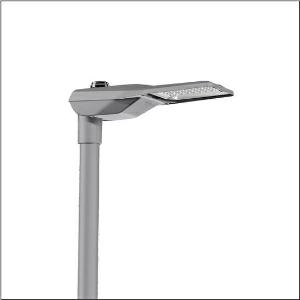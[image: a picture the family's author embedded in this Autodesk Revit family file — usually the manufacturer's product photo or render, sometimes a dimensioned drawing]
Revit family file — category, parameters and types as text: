
# Revit family: streetlight_sl_21_mini___st1_0a_5xe6d37n08jb_4401
name_source: partatom
category: Lighting Fixtures
units: mm (PartAtom-declared; Revit-internal decimal feet)

## family parameters
Cut with Voids When Loaded = No
Host = Face
Light Source = No
Part Type = Normal
Room Calculation Point = No
Round Connector Dimension = Use Diameter
Shared = No

## types (1)
- --- (1 x LED, 12830 lm, 87.3 W, 3000K)
    Apparent Load = 87 VA
    CIE Flux Codes = 40 73 97 100 100
    Color Rendering = 70
    Color Temperature = 3000K
    Default Elevation = 1800 mm
    Description = Streetlight SL 21 mini, mast luminaire, primary light control with lens, of PMMA, primary optical cover: cover, of toughened safety glass, transparent, light distribution: ST1.0a, light emission: direct distribution, primary light characteristic: asymmetric, installation type: side-entry, LED, 3G 2.5mm², High Power LED, rated luminous flux: 12.830lm, luminous efficacy: 147lm/W, light colour: 730, colour temperature: 3000K, control gear: NEMA (7pin), control: overheat protection, pre-setting: linear dimming characteristic, constant luminous flux control, time-dependent luminous flux control, flexible luminous flux parameterisation, mains connection: 230..240V, AC, 50/60Hz, connection cable pre-assembled, cable length: 10,5m, wiring characteristics: H05VV-F, start of lifetime: 87W, end of service life: 90W, reduction: 40W, luminaire housing, of diecast aluminium (EN AC-44300), powder-coated, SITECO metallic grey (DB 702S), corrosivity category C5 high according to DIN EN ISO 12944, multi-level sealing system, sealing non-destructively replaceable, inclination adjustable: 0°, 5°, 10°, 15°, length: 628mm, width: 235mm, height: 110mm, spigot size: 42mm (side-entry), mounting height: 4..8m, protection rating (complete): IP66, insulation class (complete): insulation class I (protective earthing), certification: CE, ENEC, ENEC+, VDE, impact resistance: IK10, permissible operating ambient temperature for outdoor applications: -40..+50°C, standard-compliant lighting for roads and squares, packaging unit: 1 piece

Light Distribution: ST1.0a
    Height = 110 mm
    Lamp = 1 x LED
    Lamp Light Flux = 12830 lm
    Lamp Power = 87.3 W
    Lamp count = 1
    Length = 625 mm
    Luminous efficacy = 147 lm/W
    Manufacturer = Siteco
    ModVariant = No
    Model = 5XE6D37N08JB
    Mounting Place = Pole
    Mounting Type = Pole top
    Number of Poles = 1
    OnlyDefault = Yes
    Power Factor = 1
    Product Name = Streetlight SL 21 mini | ST1.0a
    Product group = mast luminaire | pylon top
    ProductGroupID = 6100
    Protection Class = Protection class I
    Protection Degree = IP 66
    RLX_Detail_Level = 1
    RLX_Emergency_Light_Flux = 0 lm
    RLX_Emergency_Type = 0
    RLX_Emergency_Type_DB = No
    RlxData = <blob elided: 26053 chars, md5=8ca12cea>
    Socket = socket
    Standby Power = 0 W
    System Light Flux = 12830 lm
    System Power = 87 W
    Type Comments = factory setting: luminous flux: 100 % | dim-lin: 254 | 915 mA
    Type Image = l_1294379.jpg
    URL = http://relux.com
    VarID = @adj_136413
    Voltage = 0 V
    Weight = 0.00 kg
    Width = 234 mm

## geometry (parser evidence)
native form markers: Blend x4, Sweep x10
no freeform markers — native parametric forms only
